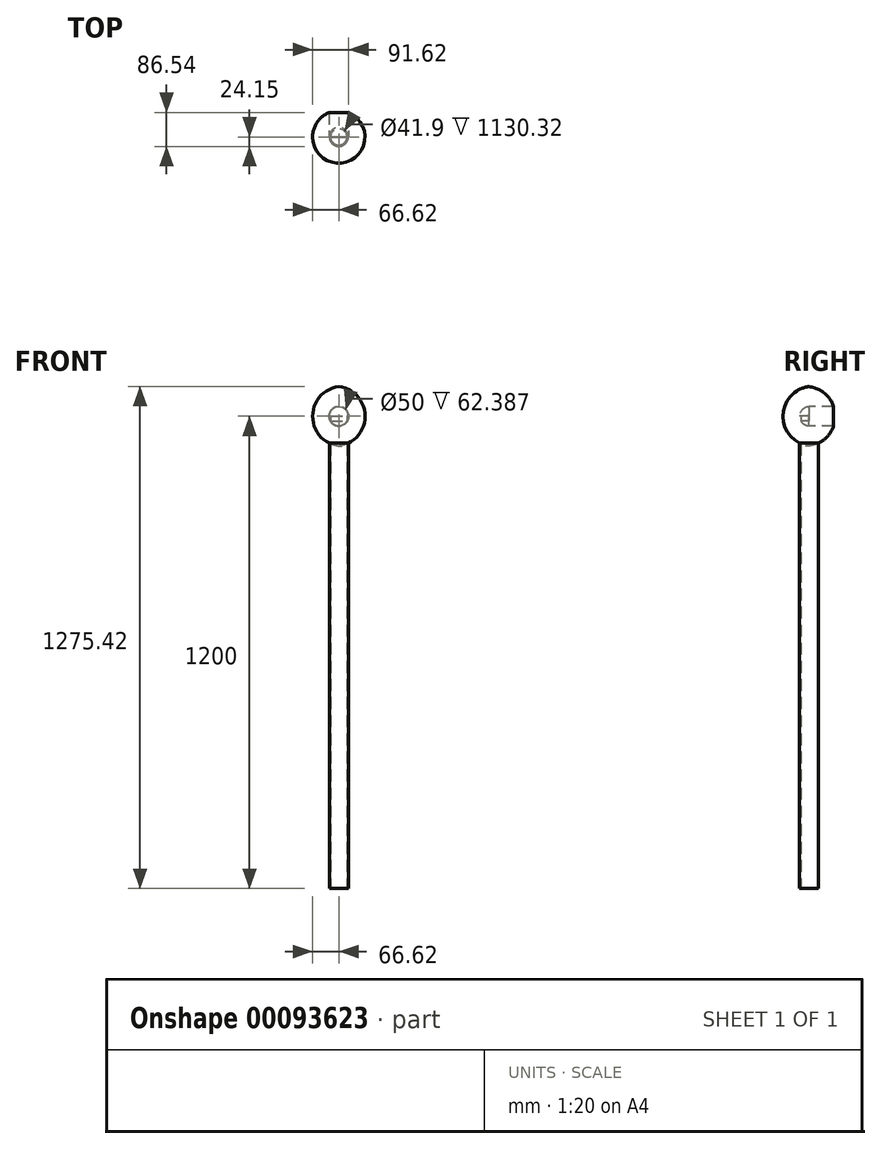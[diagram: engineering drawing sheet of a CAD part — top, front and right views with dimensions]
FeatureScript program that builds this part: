
annotation { "Feature Type Name" : "Feature", "Feature Type Description" : "" }
export const myFeature = defineFeature(function(context is Context, id is Id, definition is map)
    precondition{}
    {
        {
            var Q0;
            Q0=qCreatedBy(makeId("Top.planeOp"),FACE);
            var sketch = newSketch(context, id + "F0", { "sketchPlane" : qUnion([Q0])});
            skCircle(sketch, "E0", {"center": v(0, 0) * mm, "radius": 24.15 * mm});
            skCircle(sketch, "E1", {"center": v(0, 0) * mm, "radius": 20.95 * mm});
            skSolve(sketch);
        }
        {
            var Q0;
            Q0=makeQuery(id+"F0.imprint","IMPRINT",FACE,{"disambiguationData":[TD([[makeQuery(id+"F0.imprint","IMPRINT",EDGE,{"derivedFrom":sQuery(id+"F0.wireOp",EDGE,"E0")}),1.0]])]});
            extrude(context, id + "F1", {"entities" : qUnion([Q0]), "depth" : 1200 * mm});
        }
        {
            var Q0;
            Q0=qCreatedBy(makeId("Front.planeOp"),FACE);
            var sketch = newSketch(context, id + "F2", { "sketchPlane" : qUnion([Q0])});
            skLineSegment(sketch, "E2", {"start": v(0, 1275.42) * mm, "end": v(0, 1124.58) * mm});
            skArc(sketch, "E3", {"start": v(0, 1124.58) * mm, "mid": v(66.62, 1200) * mm, "end": v(0, 1275.42) * mm});
            skLineSegment(sketch, "E4", {"start": v(0, 0) * mm, "end": v(0, 1200) * mm, "construction": true});
            skCircle(sketch, "E5", {"center": v(0, 1200) * mm, "radius": 24.15 * mm});
            skSolve(sketch);
        }
        {
            var Q0;
            Q0=makeQuery(id+"F2.imprint","IMPRINT",FACE,{"disambiguationData":[TD([[makeQuery(id+"F2.imprint","IMPRINT",EDGE,{"derivedFrom":sQuery(id+"F2.wireOp",EDGE,"E2")}),1.0]])]});
            var Q1;
            Q1=sQuery(id+"F2.wireOp",EDGE,"E2");
            revolve(context, id + "F3", {"operationType" : NewBodyOperationType.ADD, "entities" : qUnion([Q0]), "axis" : qUnion([Q1]), "revolveType" : RevolveType.FULL});
        }
        {
            var Q0;
            Q0=sQuery(id+"F2.wireOp",VERTEX,"E4.end");
            var Q1;
            Q1=makeQuery(id+"F1.opExtrude","SWEPT_BODY",BODY,{"disambiguationData":[OSD([sQuery(id+"F0.wireOp",EDGE,"E0"),sQuery(id+"F0.wireOp",EDGE,"E1")])]});
            hole(context, id + "F4", {"style" : HoleStyle.SIMPLE, "endStyle" : HoleEndStyle.THROUGH, "holeDiameter" : 50 * mm, "locations" : qUnion([Q0]), "scope" : qUnion([Q1]), "isTappedThrough" : true});
        }
    });
